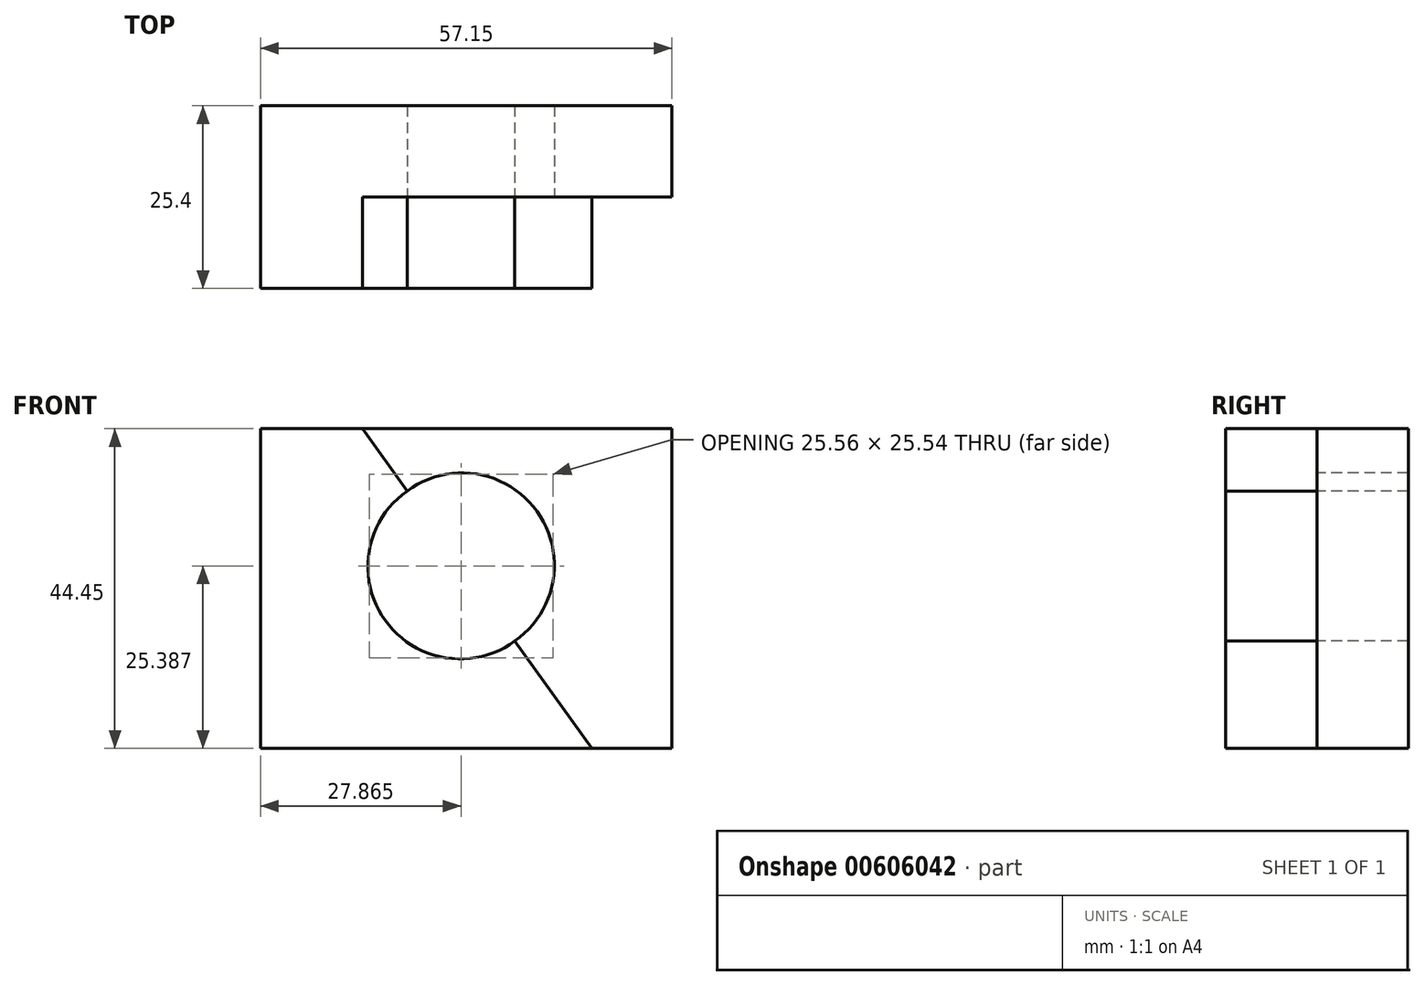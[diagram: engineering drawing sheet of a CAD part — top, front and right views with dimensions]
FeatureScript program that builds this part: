
annotation { "Feature Type Name" : "Feature", "Feature Type Description" : "" }
export const myFeature = defineFeature(function(context is Context, id is Id, definition is map)
    precondition{}
    {
        {
            var Q0;
            Q0=qCreatedBy(makeId("Front.planeOp"),FACE);
            var sketch = newSketch(context, id + "F0", { "sketchPlane" : qUnion([Q0])});
            skLineSegment(sketch, "E0", {"start": v(-55.04, 29.5) * mm, "end": v(-55.04, -14.94) * mm});
            skLineSegment(sketch, "E1", {"start": v(-55.04, -14.94) * mm, "end": v(2.1, -14.94) * mm});
            skLineSegment(sketch, "E2", {"start": v(2.1, -14.94) * mm, "end": v(2.1, 29.5) * mm});
            skLineSegment(sketch, "E3", {"start": v(2.1, 29.5) * mm, "end": v(-55.04, 29.5) * mm});
            skSolve(sketch);
        }
        {
            var Q0;
            Q0=makeQuery(id+"F0.imprint","IMPRINT",FACE,{"disambiguationData":[TD([[makeQuery(id+"F0.imprint","IMPRINT",EDGE,{"derivedFrom":sQuery(id+"F0.wireOp",EDGE,"E0")}),1.0]])]});
            extrude(context, id + "F1", {"entities" : qUnion([Q0]), "depth" : 25.4 * mm, "offsetDistance" : 25.4 * mm});
        }
        {
            var Q0;
            Q0=makeQuery(id+"F1.opExtrude","CAP_FACE",FACE,{"disambiguationData":[OSD([sQuery(id+"F0.wireOp",EDGE,"E0"),sQuery(id+"F0.wireOp",EDGE,"E1"),sQuery(id+"F0.wireOp",EDGE,"E2"),sQuery(id+"F0.wireOp",EDGE,"E3")])],"isStart":false});
            var sketch = newSketch(context, id + "F2", { "sketchPlane" : qUnion([Q0])});
            skLineSegment(sketch, "E4", {"start": v(-40.89, 29.5) * mm, "end": v(-9, -14.94) * mm});
            skSolve(sketch);
        }
        {
            var Q0;
            {var subQ0=sQuery(id+"F2.wireOp",EDGE,"E4");Q0=makeQuery(id+"F2.imprint","IMPRINT",FACE,{"disambiguationData":[TD([[makeQuery(id+"F2.imprint","IMPRINT",EDGE,{"derivedFrom":subQ0}),1.0]])]});}
            extrude(context, id + "F3", {"entities" : qUnion([Q0]), "operationType" : NewBodyOperationType.REMOVE, "oppositeDirection" : true, "depth" : 12.7 * mm, "offsetDistance" : 25.4 * mm});
        }
        {
            var Q0;
            Q0=makeQuery(id+"F1.opExtrude","CAP_FACE",FACE,{"disambiguationData":[OSD([sQuery(id+"F0.wireOp",EDGE,"E0"),sQuery(id+"F0.wireOp",EDGE,"E1"),sQuery(id+"F0.wireOp",EDGE,"E2"),sQuery(id+"F0.wireOp",EDGE,"E3")])],"isStart":false});
            var sketch = newSketch(context, id + "F4", { "sketchPlane" : qUnion([Q0])});
            skArc(sketch, "E5", {"start": v(-34.68, 20.86) * mm, "mid": v(-37.73, 2.87) * mm, "end": v(-19.71, 0) * mm});
            skSolve(sketch);
        }
        {
            var Q0;
            {var subQ0=sQuery(id+"F4.wireOp",EDGE,"E5");Q0=makeQuery(id+"F4.imprint","IMPRINT",FACE,{"disambiguationData":[TD([[makeQuery(id+"F4.imprint","IMPRINT",EDGE,{"derivedFrom":subQ0}),1.0]])]});}
            extrude(context, id + "F5", {"entities" : qUnion([Q0]), "operationType" : NewBodyOperationType.REMOVE, "endBound" : BoundingType.THROUGH_ALL, "oppositeDirection" : true, "depth" : 25.4 * mm, "offsetDistance" : 25.4 * mm});
        }
        {
            var Q0;
            Q0=makeQuery(id+"F3.boolean.opBoolean","COPY",FACE,{"derivedFrom":makeQuery(id+"F3.opExtrude","CAP_FACE",FACE,{"disambiguationData":[OSD([sQuery(id+"F0.wireOp",EDGE,"E1"),sQuery(id+"F0.wireOp",EDGE,"E2"),sQuery(id+"F0.wireOp",EDGE,"E3"),sQuery(id+"F2.wireOp",EDGE,"E4")])],"isStart":false})});
            var sketch = newSketch(context, id + "F6", { "sketchPlane" : qUnion([Q0])});
            skArc(sketch, "E6", {"start": v(-19.71, 0) * mm, "mid": v(-16.61, 18.02) * mm, "end": v(-34.68, 20.86) * mm});
            skSolve(sketch);
        }
        {
            var Q0;
            Q0=makeQuery(id+"F6.imprint","IMPRINT",FACE,{"disambiguationData":[TD([[makeQuery(id+"F6.imprint","IMPRINT",EDGE,{"derivedFrom":sQuery(id+"F6.wireOp",EDGE,"E6")}),1.0]])]});
            extrude(context, id + "F7", {"entities" : qUnion([Q0]), "operationType" : NewBodyOperationType.REMOVE, "oppositeDirection" : true, "depth" : 25.4 * mm, "offsetDistance" : 25.4 * mm});
        }
    });
